# Revit family: Specialty_Equipment-Fiberstone_Planter-Planters_Unlimited-Lynx-Round-rev
name_source: partatom
category: Specialty Equipment
units: mm (PartAtom-declared; Revit-internal decimal feet)

## family parameters
Always vertical = Yes
Cut with Voids When Loaded = No
Enable Cutting in Views = No
Maintain Annotation Orientation = No
OmniClass Number = 23.40.05.21.17
OmniClass Title = Planters
Part Type = Normal
Room Calculation Point = No
Round Connector Dimension = Use Diameter
Shared = No
Work Plane-Based = No

## types (7) — shared parameters
Assembly Code = G2050600
CD_Finish = Plastic-Fiberstone-Carlsbad-Chenza
CD_Microsite = https://www.caddetails.com
CD_Pad Size = 3.0"
CD_Product Page URL = https://www.plantersunlimited.com
CD_Specification = https://www.plantersunlimited.com
Default Elevation = 0.0"
Description = Lynx Round Planter
Manufacturer = Planters Unlimited
Model = Lynx Series Planters
Type Comments = Round Planter
URL = https://www.plantersunlimited.com

## per-type parameters (varying)
| type | CD_Diameter | CD_Height | CD_Pad Spacing | CD_Planter Belt1 | CD_Planter Belt2 | CD_Planter Lip | CD_Radius | CD_Radius Baseplate |
| 18.5"Dia x 13"H | 18.5" | 13.0" | 5.0" | 0.4" | 0.5" | 0.9" | 9.3" | 6.0" |
| 20"Dia x 16"H | 20.0" | 16.0" | 5.7" | 0.4" | 0.6" | 1.0" | 10.0" | 6.7" |
| 23"Dia x 16"H | 23.0" | 16.0" | 7.2" | 0.5" | 0.7" | 1.2" | 11.5" | 8.2" |
| 25"Dia x 19"H | 25.0" | 19.0" | 8.2" | 0.6" | 0.8" | 1.3" | 12.5" | 9.2" |
| 30"Dia x 22.5"H | 30.0" | 22.5" | 10.7" | 0.8" | 1.1" | 1.5" | 15.0" | 11.7" |
| 35"Dia x 25"H | 35.0" | 25.0" | 13.2" | 0.9" | 1.3" | 1.8" | 17.5" | 14.2" |
| 42"Dia x 32"H | 42.0" | 32.0" | 16.7" | 1.2" | 1.6" | 2.1" | 21.0" | 17.7" |

## geometry (parser evidence)
native form markers: Sweep x2
no freeform markers — native parametric forms only
